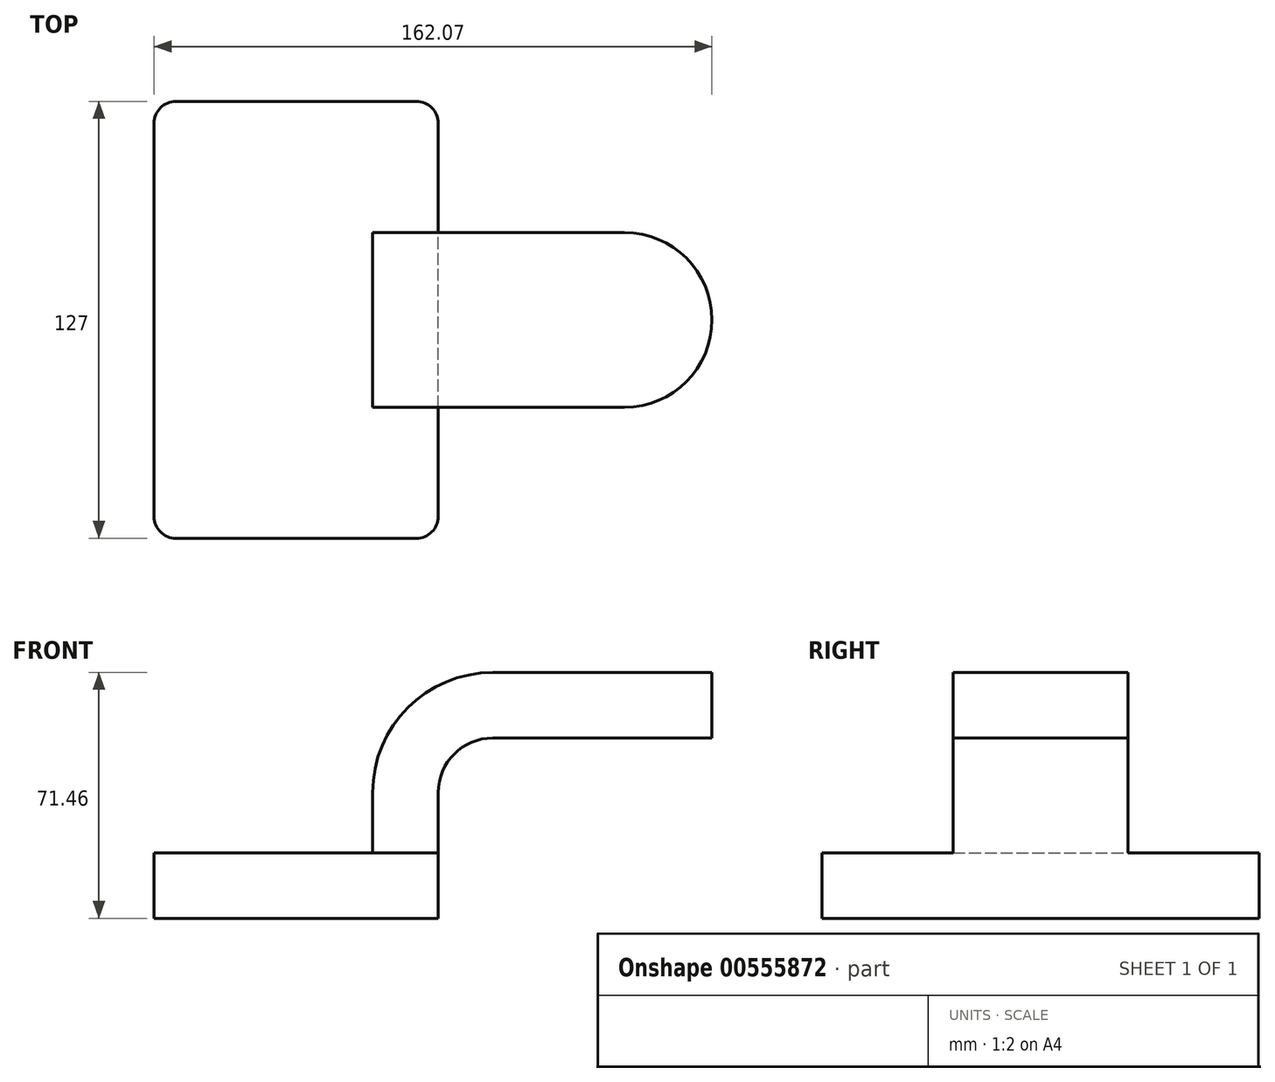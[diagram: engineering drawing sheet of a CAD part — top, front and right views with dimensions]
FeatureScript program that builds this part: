
annotation { "Feature Type Name" : "Feature", "Feature Type Description" : "" }
export const myFeature = defineFeature(function(context is Context, id is Id, definition is map)
    precondition{}
    {
        {
            var Q0;
            Q0=qCreatedBy(makeId("Front.planeOp"),FACE);
            var sketch = newSketch(context, id + "F0", { "sketchPlane" : qUnion([Q0])});
            skLineSegment(sketch, "E0.bottom", {"start": v(41.27, 9.53) * mm, "end": v(-41.28, 9.53) * mm});
            skLineSegment(sketch, "E0.top", {"start": v(41.28, -9.52) * mm, "end": v(-41.27, -9.52) * mm});
            skLineSegment(sketch, "E0.left", {"start": v(41.28, 9.53) * mm, "end": v(41.28, -9.52) * mm});
            skLineSegment(sketch, "E0.right", {"start": v(-41.28, 9.53) * mm, "end": v(-41.27, -9.52) * mm});
            skPoint(sketch, "E0.middle", {"position": v(0, 0) * mm});
            skLineSegment(sketch, "E1.bottom", {"start": v(60.32, 38.1) * mm, "end": v(111.12, 38.1) * mm});
            skLineSegment(sketch, "E1.top", {"start": v(60.32, 66.68) * mm, "end": v(111.12, 66.68) * mm});
            skLineSegment(sketch, "E1.left", {"start": v(60.32, 38.1) * mm, "end": v(60.32, 66.68) * mm});
            skLineSegment(sketch, "E1.right", {"start": v(111.12, 38.1) * mm, "end": v(111.12, 66.68) * mm});
            skPoint(sketch, "E1.middle", {"position": v(85.72, 52.39) * mm});
            skLineSegment(sketch, "E2", {"start": v(41.27, 9.53) * mm, "end": v(41.27, 27) * mm});
            skArc(sketch, "E3", {"start": v(41.27, 27) * mm, "mid": v(45.92, 38.23) * mm, "end": v(57.15, 42.88) * mm});
            skLineSegment(sketch, "E4", {"start": v(57.15, 42.88) * mm, "end": v(95.4, 42.88) * mm});
            skLineSegment(sketch, "E5.0", {"start": v(57.15, 61.93) * mm, "end": v(95.4, 61.93) * mm});
            skArc(sketch, "E5.1", {"start": v(22.23, 27) * mm, "mid": v(32.45, 51.7) * mm, "end": v(57.15, 61.93) * mm});
            skLineSegment(sketch, "E5.2", {"start": v(22.23, 9.53) * mm, "end": v(22.23, 27) * mm});
            skLineSegment(sketch, "E6", {"start": v(95.4, 38.1) * mm, "end": v(95.4, 66.68) * mm});
            skFitSpline(sketch, "E7", {"points": [v(-41.28, 9.52) * mm, v(57.15, 61.93) * mm], "startDerivative": vector(-0.31, 94.32) * mm, "endDerivative": vector(162.13, -1.46) * mm});
            skSolve(sketch);
        }
        {
            var Q0;
            Q0=makeQuery(id+"F0.imprint","IMPRINT",FACE,{"disambiguationData":[TD([[makeQuery(id+"F0.imprint","IMPRINT",EDGE,{"derivedFrom":sQuery(id+"F0.wireOp",EDGE,"E0.top")}),-1.0]])]});
            extrude(context, id + "F1", {"entities" : qUnion([Q0]), "endBound" : BoundingType.SYMMETRIC, "depth" : 127 * mm, "offsetDistance" : 25.4 * mm});
        }
        {
            var Q0;
            {var subQ1=sQuery(id+"F0.wireOp",EDGE,"E2");Q0=makeQuery(id+"F0.imprint","IMPRINT",FACE,{"disambiguationData":[TD([[makeQuery(id+"F0.imprint","IMPRINT",EDGE,{"derivedFrom":subQ1}),1.0]])]});}
            var Q1;
            {var subQ0=sQuery(id+"F0.wireOp",EDGE,"E4");var subQ1=sQuery(id+"F0.wireOp",EDGE,"E1.left");var subQ2=makeQuery(id+"F0.imprint","INTERSECT",VERTEX,{"derivedFrom":[subQ1,subQ0]});Q1=makeQuery(id+"F0.imprint","IMPRINT",FACE,{"disambiguationData":[TD([[makeQuery(id+"F0.imprint","IMPRINT",EDGE,{"disambiguationData":[TD([[subQ2,-1.0]])],"derivedFrom":subQ1}),-1.0]])]});}
            extrude(context, id + "F2", {"entities" : qUnion([Q0, Q1]), "operationType" : NewBodyOperationType.ADD, "endBound" : BoundingType.SYMMETRIC, "depth" : 50.8 * mm, "offsetDistance" : 25.4 * mm});
        }
        {
            var Q0;
            Q0=makeQuery(id+"F0.imprint","IMPRINT",FACE,{"disambiguationData":[TD([[makeQuery(id+"F0.imprint","IMPRINT",EDGE,{"derivedFrom":sQuery(id+"F0.wireOp",EDGE,"E5.1")}),1.0]])]});
            extrude(context, id + "F3", {"entities" : qUnion([Q0]), "operationType" : NewBodyOperationType.ADD, "endBound" : BoundingType.SYMMETRIC, "depth" : 15.88 * mm, "offsetDistance" : 25.4 * mm});
        }
        {
            var Q0;
            Q0=makeQuery(id+"F2.opExtrude","SWEPT_FACE",FACE,{"disambiguationData":[OSD([sQuery(id+"F0.wireOp",EDGE,"E6")])]});
            var sketch = newSketch(context, id + "F4", { "sketchPlane" : qUnion([Q0])});
            skLineSegment(sketch, "E8", {"start": v(0, 61.93) * mm, "end": v(0, 42.88) * mm});
            skSolve(sketch);
        }
        {
            var Q0;
            {var subQ0=sQuery(id+"F4.wireOp",EDGE,"E8");Q0=makeQuery(id+"F4.imprint","IMPRINT",FACE,{"disambiguationData":[TD([[makeQuery(id+"F4.imprint","IMPRINT",EDGE,{"derivedFrom":subQ0}),-1.0]])]});}
            var Q1;
            Q1=sQuery(id+"F4.wireOp",EDGE,"E8");
            revolve(context, id + "F5", {"operationType" : NewBodyOperationType.ADD, "entities" : qUnion([Q0]), "axis" : qUnion([Q1]), "revolveType" : RevolveType.FULL});
        }
        {
            var Q0;
            Q0=makeQuery(id+"F1.opExtrude","CAP_EDGE",EDGE,{"disambiguationData":[OSD([sQuery(id+"F0.wireOp",EDGE,"E0.left")])],"isStart":false});
            var Q1;
            Q1=makeQuery(id+"F1.opExtrude","CAP_EDGE",EDGE,{"disambiguationData":[OSD([sQuery(id+"F0.wireOp",EDGE,"E0.left")])],"isStart":true});
            var Q2;
            Q2=makeQuery(id+"F1.opExtrude","CAP_EDGE",EDGE,{"disambiguationData":[OSD([sQuery(id+"F0.wireOp",EDGE,"E0.right")])],"isStart":true});
            var Q3;
            Q3=makeQuery(id+"F1.opExtrude","CAP_EDGE",EDGE,{"disambiguationData":[OSD([sQuery(id+"F0.wireOp",EDGE,"E0.right")])],"isStart":false});
            fillet(context, id + "F6", {"entities" : qUnion([Q0, Q1, Q2, Q3]), "radius" : 6.35 * mm, "tangentPropagation" : true, "allowEdgeOverflow" : false});
        }
    });
